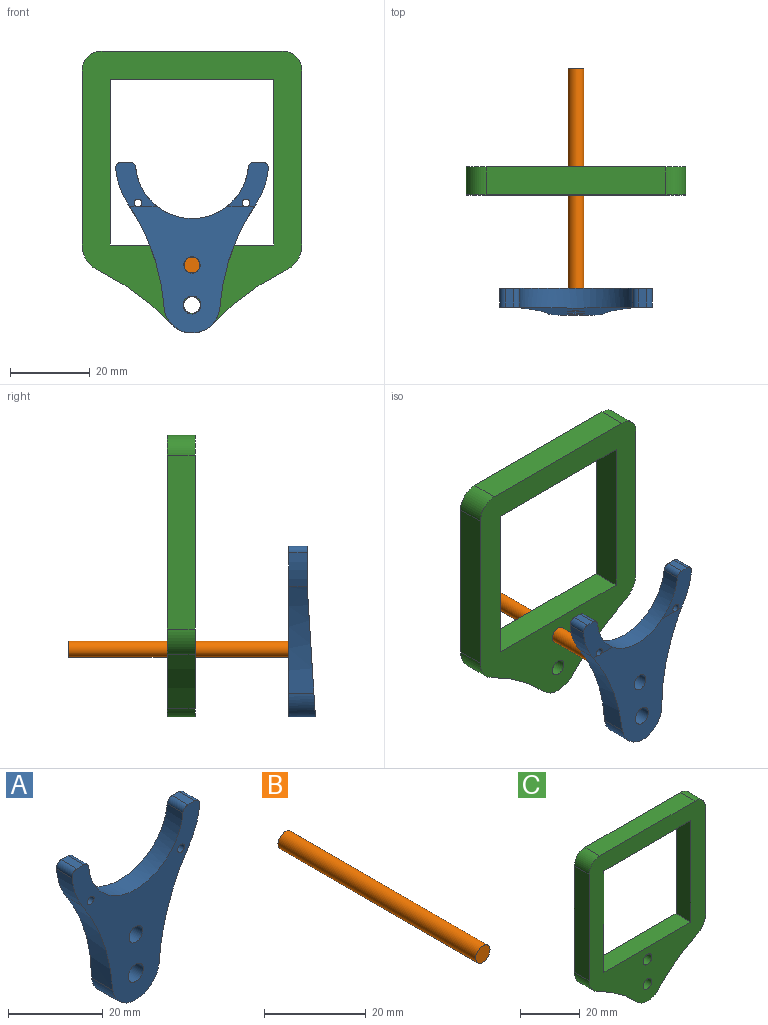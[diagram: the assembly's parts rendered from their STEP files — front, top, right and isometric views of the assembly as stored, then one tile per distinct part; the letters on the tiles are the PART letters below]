
ASSEMBLY  parts=3 mates=2
PART A: 20 faces, bbox 38.9x7.4x43.5 mm
  f0: plane 11.13x10.34mm, normal (0,1,0), area 57.1mm2, adj f2,f8,f9,f10,f11,f12,f13,f19
  f1: plane 11.13x10.34mm, normal (0,1,0), area 57.1mm2, adj f3,f4,f5,f6,f7,f8,f14,f19
  f2: cylinder r=52.72mm len=26.55mm, axis (0,-1,0), area 155.9mm2, adj f0,f13,f15,f16,f19
  f3: cylinder r=52.72mm len=26.55mm, axis (0,-1,0), area 155.9mm2, adj f1,f4,f15,f16,f19
  f4: cylinder r=19.15mm len=8.62mm, axis (0,-1,0), area 43.2mm2, adj f1,f3,f5,f15
  f5: cylinder r=1.5mm len=4.7mm, axis (0,-1,0), area 11.7mm2, adj f1,f4,f6,f15
  f6: plane 4.7x2.01mm, normal (0,0,1), area 9.4mm2, adj f1,f5,f7,f15
  f7: cylinder r=1.5mm len=4.7mm, axis (0,-1,0), area 10.4mm2, adj f1,f6,f8,f15
  f8: cylinder r=14.15mm len=28.17mm, axis (0,-1,0), area 196.2mm2, adj f0,f1,f7,f9,f15,f19
  f9: cylinder r=1.5mm len=4.7mm, axis (0,-1,0), area 10.4mm2, adj f0,f8,f10,f15
  f10: plane 4.7x2.01mm, normal (0,0,1), area 9.4mm2, adj f0,f9,f11,f15
  f11: cylinder r=1.5mm len=4.7mm, axis (0,-1,0), area 11.7mm2, adj f0,f10,f13,f15
  f12: cylinder r=1mm len=4.71mm, axis (0,-1,0), area 29.5mm2, adj f0,f15,f19
  f13: cylinder r=19.15mm len=8.62mm, axis (0,-1,0), area 43.2mm2, adj f0,f2,f11,f15
  f14: cylinder r=1mm len=4.71mm, axis (0,-1,0), area 29.5mm2, adj f1,f15,f19
  f15: plane 42.75x38.17mm, normal (0,-1,0), area 624.8mm2, adj f2,f3,f4,f5,f6,f7,f8,f9
  f16: cylinder r=7mm len=13.84mm, axis (0,-1,0), area 125.5mm2, adj f2,f3,f15,f19
  f17: cylinder r=2.05mm len=5.75mm, axis (0,-1,0), area 72.4mm2, adj f15,f19
  f18: cylinder r=2.25mm len=6.39mm, axis (0,-1,0), area 88.3mm2, adj f15,f19
  f19: plane 32.37x31.91mm, normal (0,1,0.06), area 511.5mm2, adj f0,f1,f2,f3,f8,f12,f14,f16
PART B: 3 faces, bbox 4x55x4 mm
  f0: cylinder r=2mm len=55mm, axis (0,-1,0), area 691.2mm2, adj f1,f2
  f1: plane 4x4mm, normal (0,1,0), area 12.6mm2, adj f0
  f2: plane 4x4mm, normal (0,-1,0), area 12.6mm2, adj f0
PART C: 25 faces, bbox 55x7x70.5 mm
  f0: plane 4.98x3.5mm, normal (-1,0,0), area 17.4mm2, adj f1,f5,f22,f24
  f1: plane 4.31x3.5mm, normal (-0.5,0,0.87), area 17.4mm2, adj f0,f2,f22,f24
  f2: plane 4.31x3.5mm, normal (0.5,0,0.87), area 17.4mm2, adj f1,f3,f22,f24
  f3: plane 4.98x3.5mm, normal (1,0,0), area 17.4mm2, adj f2,f4,f22,f24
  f4: plane 4.31x3.5mm, normal (0.5,0,-0.87), area 17.4mm2, adj f3,f5,f22,f24
  f5: plane 4.31x3.5mm, normal (-0.5,0,-0.87), area 17.4mm2, adj f0,f4,f22,f24
  f6: plane 41x7mm, normal (0,0,-1), area 287mm2, adj f7,f20,f21,f22
  f7: plane 41.5x7mm, normal (-1,0,0), area 290.5mm2, adj f6,f8,f21,f22
  f8: plane 41x7mm, normal (0,0,1), area 287mm2, adj f7,f20,f21,f22
  f9: plane 43.5x7mm, normal (1,0,0), area 304.5mm2, adj f10,f19,f21,f22
  f10: cylinder r=5mm len=7mm, axis (0,1,0), area 55mm2, adj f9,f11,f21,f22
  f11: plane 45x7mm, normal (0,0,1), area 315mm2, adj f10,f12,f21,f22
  f12: cylinder r=5mm len=7mm, axis (0,1,0), area 55mm2, adj f11,f13,f21,f22
  f13: plane 43.5x7mm, normal (-1,0,0), area 304.5mm2, adj f12,f14,f21,f22
  f14: cylinder r=7mm len=7mm, axis (0,1,0), area 55.5mm2, adj f13,f15,f21,f22
  f15: cylinder r=62.74mm len=18.56mm, axis (0,1,0), area 162.2mm2, adj f14,f16,f21,f22
  f16: cylinder r=7mm len=9.83mm, axis (0,1,0), area 76.3mm2, adj f15,f17,f21,f22
  f17: cylinder r=62.74mm len=18.56mm, axis (0,1,0), area 162.2mm2, adj f16,f19,f21,f22
  f18: cylinder r=2.05mm len=7mm, axis (0,1,0), area 90.2mm2, adj f21,f22
  f19: cylinder r=7mm len=7mm, axis (0,1,0), area 55.5mm2, adj f9,f17,f21,f22
  f20: plane 41.5x7mm, normal (1,0,0), area 290.5mm2, adj f6,f8,f21,f22
  f21: plane 70.5x55mm, normal (0,-1,0), area 1631.3mm2, adj f6,f7,f8,f9,f10,f11,f12,f13
  f22: plane 70.5x55mm, normal (0,1,0), area 1580.2mm2, adj f0,f1,f2,f3,f4,f5,f6,f7
  f23: cylinder r=2.05mm len=4.1mm, axis (0,1,0), area 45.1mm2, adj f21,f24
  f24: plane 9.95x8.62mm, normal (0,1,0), area 51.1mm2, adj f0,f1,f2,f3,f4,f5,f23
PLACE A rot(axis=(0,0,1),180deg) t=(7.87,-19.52,23.95)mm
PLACE B t=(7.87,-19.52,-1.8)mm
PLACE C rot(axis=(0,-1,0),0deg) t=(7.87,7.32,23.95)mm
MATE fastened B.f0 <-> A.f17  axis (0,-1,0) through (7.87,-19.52,-1.8)mm
MATE slider B.f0 <-> C.f18  axis (0,-1,0) through (7.87,7.98,-1.8)mm
